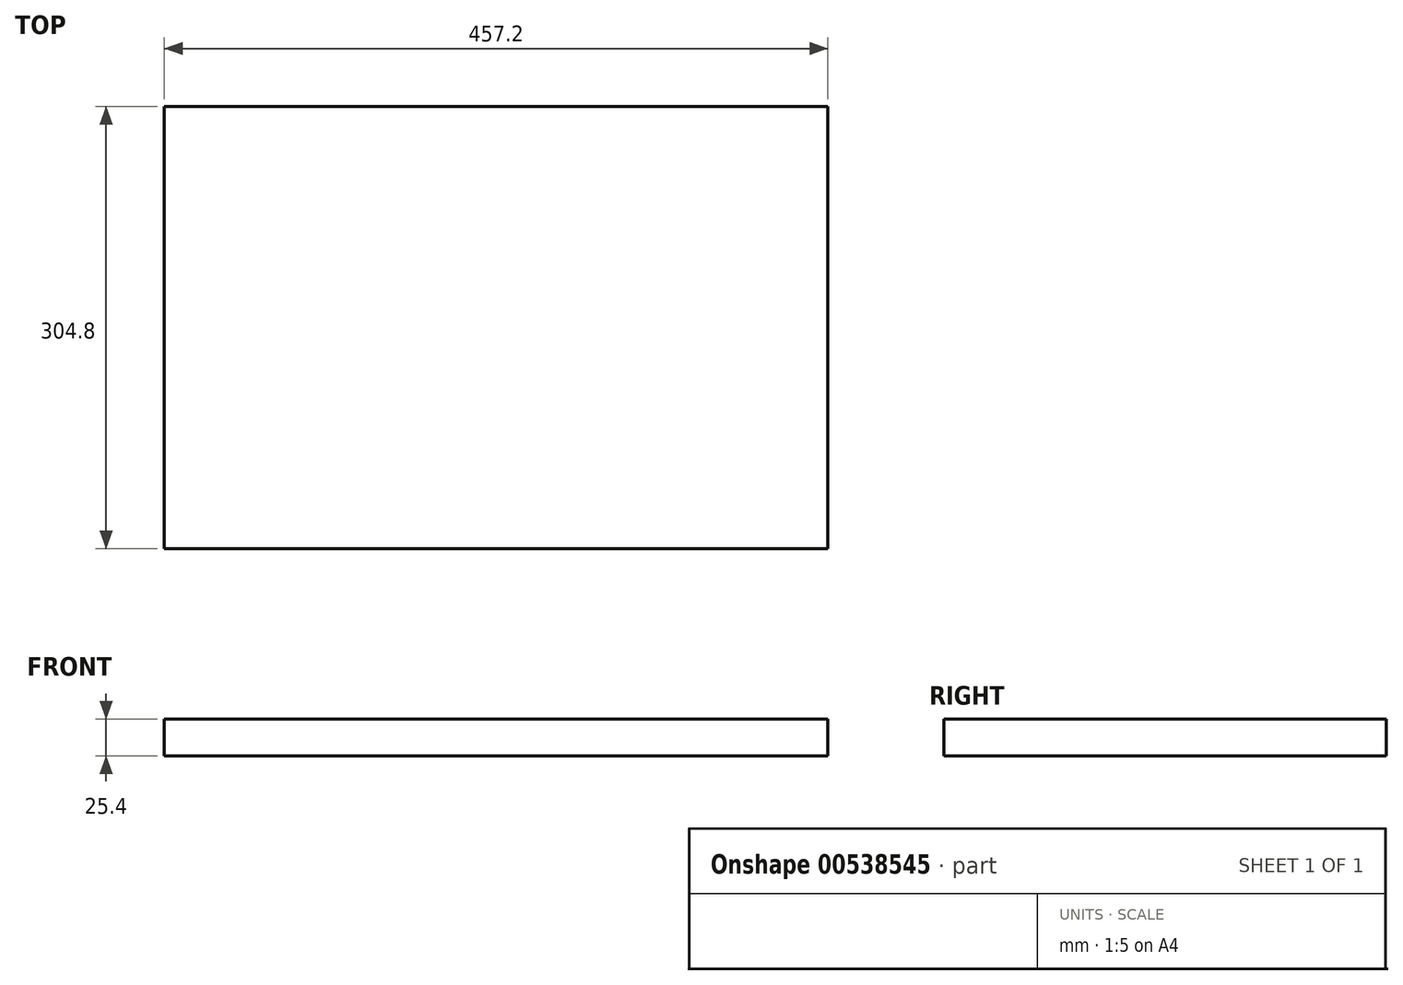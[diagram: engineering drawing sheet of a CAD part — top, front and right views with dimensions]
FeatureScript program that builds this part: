
annotation { "Feature Type Name" : "Feature", "Feature Type Description" : "" }
export const myFeature = defineFeature(function(context is Context, id is Id, definition is map)
    precondition{}
    {
        {
            var Q0;
            Q0=qCreatedBy(makeId("Front.planeOp"),FACE);
            var sketch = newSketch(context, id + "F0", { "sketchPlane" : qUnion([Q0])});
            skLineSegment(sketch, "E0.bottom", {"start": v(-228.6, -2.54) * mm, "end": v(228.6, -2.54) * mm});
            skLineSegment(sketch, "E0.top", {"start": v(-228.6, -27.94) * mm, "end": v(228.6, -27.94) * mm});
            skLineSegment(sketch, "E0.left", {"start": v(-228.6, -2.54) * mm, "end": v(-228.6, -27.94) * mm});
            skLineSegment(sketch, "E0.right", {"start": v(228.6, -2.54) * mm, "end": v(228.6, -27.94) * mm});
            skPoint(sketch, "E0.middle", {"position": v(0, -15.24) * mm});
            skSolve(sketch);
        }
        {
            var Q0;
            Q0=qSketchRegion(id+"F0",true);
            extrude(context, id + "F1", {"entities" : qUnion([Q0]), "depth" : 304.8 * mm, "offsetDistance" : 25.4 * mm});
        }
    });
